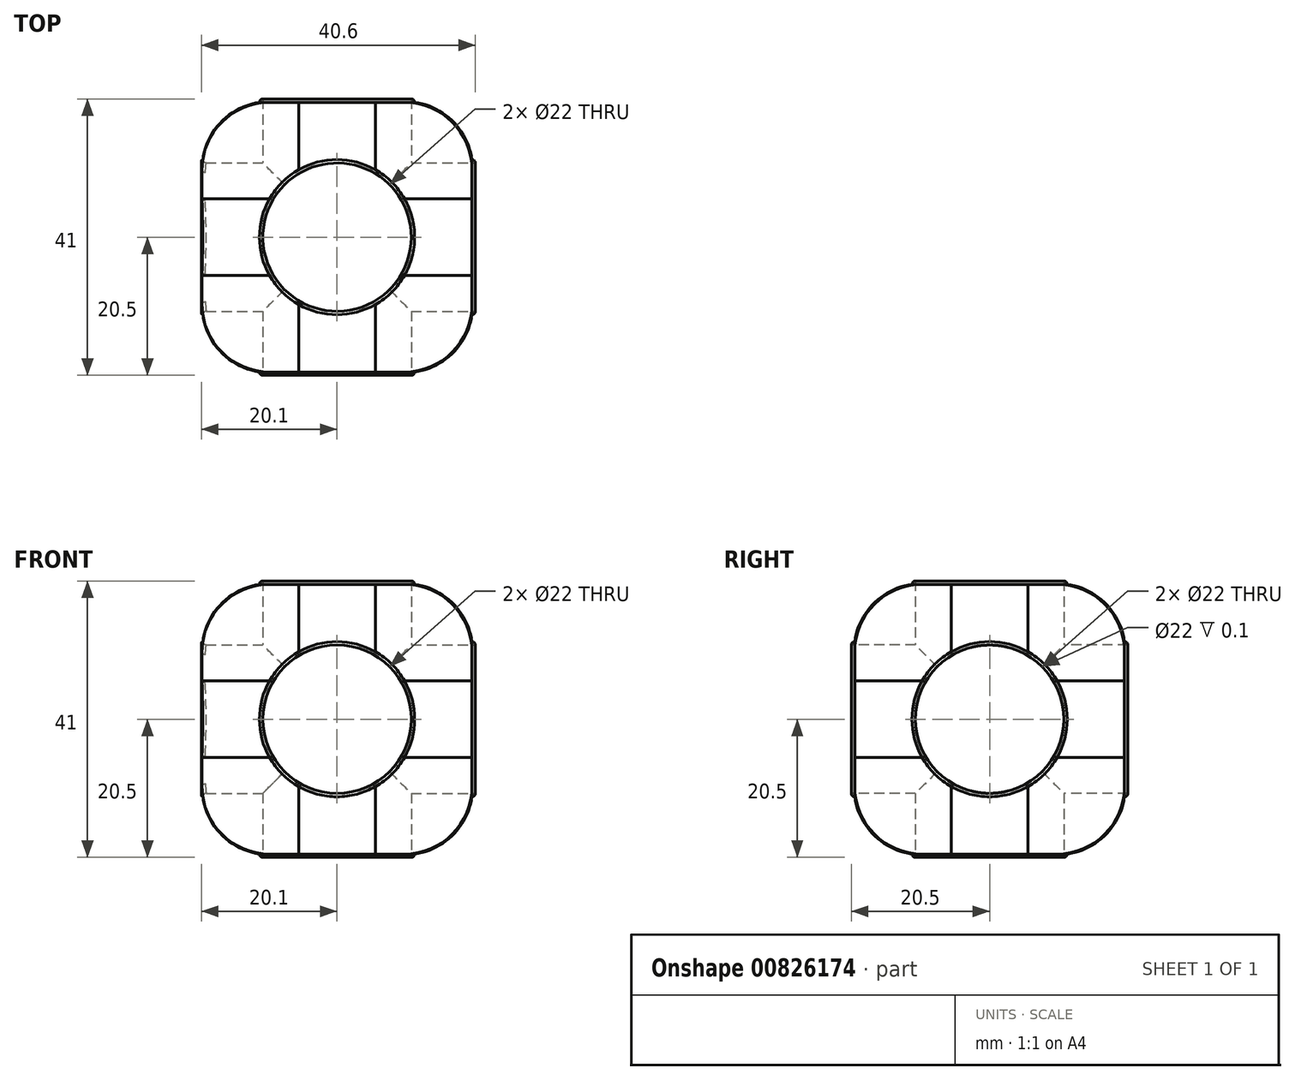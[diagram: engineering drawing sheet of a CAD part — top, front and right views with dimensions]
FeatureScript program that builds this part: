
annotation { "Feature Type Name" : "Feature", "Feature Type Description" : "" }
export const myFeature = defineFeature(function(context is Context, id is Id, definition is map)
    precondition{}
    {
        {
            var Q0;
            Q0=qCreatedBy(makeId("Top.planeOp"),FACE);
            var sketch = newSketch(context, id + "F0", { "sketchPlane" : qUnion([Q0])});
            skCircle(sketch, "E0", {"center": v(0, 0) * mm, "radius": 11 * mm});
            skLineSegment(sketch, "E1", {"start": v(0, 20) * mm, "end": v(20, 20) * mm});
            skLineSegment(sketch, "E2.MirrorCS", {"start": v(0, -20) * mm, "end": v(20, -20) * mm});
            skLineSegment(sketch, "E3", {"start": v(20, 20) * mm, "end": v(20, -20) * mm});
            skLineSegment(sketch, "E4.MirrorCS", {"start": v(-20, 20) * mm, "end": v(-20, -20) * mm});
            skLineSegment(sketch, "E5.MirrorCS", {"start": v(0, 20) * mm, "end": v(-20, 20) * mm});
            skLineSegment(sketch, "E6.MirrorCS", {"start": v(0, -20) * mm, "end": v(-20, -20) * mm});
            skPoint(sketch, "E7.orphan", {"position": v(0, 20) * mm});
            skPoint(sketch, "E8.MirrorCS.end.orphan", {"position": v(0, -20) * mm});
            skSolve(sketch);
        }
        {
            var Q0;
            Q0 = qSketchRegion(id + "F0", true);
            extrude(context, id + "F1", {"entities" : qUnion([Q0]), "depth" : 40 * mm, "offsetDistance" : 25 * mm});
        }
        {
            var Q0;
            Q0=makeQuery(id+"F1.opExtrude","SWEPT_FACE",FACE,{"disambiguationData":[OSD([sQuery(id+"F0.wireOp",EDGE,"E3")])]});
            var sketch = newSketch(context, id + "F2", { "sketchPlane" : qUnion([Q0])});
            skCircle(sketch, "E9", {"center": v(0, 20) * mm, "radius": 11 * mm});
            skPoint(sketch, "E10.orphan", {"position": v(20, 20) * mm});
            skPoint(sketch, "E11.end.orphan", {"position": v(-20, 20) * mm});
            skPoint(sketch, "E12.trimOffspring.end.orphan", {"position": v(0, 0) * mm});
            skPoint(sketch, "E13.start.orphan", {"position": v(0, 40) * mm});
            skSolve(sketch);
        }
        {
            var Q0;
            Q0 = qSketchRegion(id + "F2", true);
            var Q1;
            Q1=sQuery(id+"F2.wireOp",EDGE,"E9");
            extrude(context, id + "F3", {"entities" : qUnion([Q0]), "operationType" : NewBodyOperationType.REMOVE, "surfaceEntities" : qUnion([Q1]), "oppositeDirection" : true, "depth" : 40 * mm, "offsetDistance" : 25 * mm});
        }
        {
            var Q0;
            Q0=makeQuery(id+"F1.opExtrude","SWEPT_FACE",FACE,{"disambiguationData":[OSD([sQuery(id+"F0.wireOp",EDGE,"E2.MirrorCS"),sQuery(id+"F0.wireOp",EDGE,"E6.MirrorCS")])]});
            var sketch = newSketch(context, id + "F4", { "sketchPlane" : qUnion([Q0])});
            skCircle(sketch, "E14", {"center": v(0, 20) * mm, "radius": 11 * mm});
            skPoint(sketch, "E15.orphan", {"position": v(-20, 20) * mm});
            skPoint(sketch, "E16.end.orphan", {"position": v(20, 20) * mm});
            skPoint(sketch, "E17.start.orphan", {"position": v(0, 0) * mm});
            skPoint(sketch, "E18.trimOffspring.end.orphan", {"position": v(0, 40) * mm});
            skSolve(sketch);
        }
        {
            var Q0;
            Q0=makeQuery(id+"F4.imprint","IMPRINT",FACE,{"disambiguationData":[TD([[makeQuery(id+"F4.imprint","IMPRINT",EDGE,{"derivedFrom":sQuery(id+"F4.wireOp",EDGE,"E14")}),1.0]])]});
            var Q1;
            Q1=sQuery(id+"F4.wireOp",EDGE,"E14");
            extrude(context, id + "F5", {"entities" : qUnion([Q0]), "operationType" : NewBodyOperationType.REMOVE, "surfaceEntities" : qUnion([Q1]), "oppositeDirection" : true, "depth" : 40 * mm, "offsetDistance" : 25 * mm});
        }
        {
            var Q0;
            Q0=makeQuery(id+"F1.opExtrude","SWEPT_FACE",FACE,{"disambiguationData":[OSD([sQuery(id+"F0.wireOp",EDGE,"E4.MirrorCS")])]});
            var sketch = newSketch(context, id + "F6", { "sketchPlane" : qUnion([Q0])});
            skCircle(sketch, "E19", {"center": v(0, 20) * mm, "radius": 11 * mm});
            skCircle(sketch, "E20", {"center": v(0, 20) * mm, "radius": 11.5 * mm});
            skSolve(sketch);
        }
        {
            var Q0;
            Q0 = qSketchRegion(id + "F6", true);
            extrude(context, id + "F7", {"entities" : qUnion([Q0]), "depth" : 0.1 * mm, "offsetDistance" : 25 * mm});
        }
        {
            var Q0;
            Q0=makeQuery(id+"F1.opExtrude","SWEPT_FACE",FACE,{"disambiguationData":[OSD([sQuery(id+"F0.wireOp",EDGE,"E2.MirrorCS"),sQuery(id+"F0.wireOp",EDGE,"E6.MirrorCS")])]});
            var sketch = newSketch(context, id + "F8", { "sketchPlane" : qUnion([Q0])});
            skCircle(sketch, "E21", {"center": v(0, 20) * mm, "radius": 11 * mm});
            skCircle(sketch, "E22", {"center": v(0, 20) * mm, "radius": 11.5 * mm});
            skSolve(sketch);
        }
        {
            var Q0;
            Q0 = qSketchRegion(id + "F8", true);
            extrude(context, id + "F9", {"entities" : qUnion([Q0]), "operationType" : NewBodyOperationType.ADD, "depth" : 0.5 * mm, "offsetDistance" : 25 * mm});
        }
        {
            var Q0;
            Q0=makeQuery(id+"F1.opExtrude","SWEPT_FACE",FACE,{"disambiguationData":[OSD([sQuery(id+"F0.wireOp",EDGE,"E3")])]});
            var sketch = newSketch(context, id + "F10", { "sketchPlane" : qUnion([Q0])});
            skCircle(sketch, "E23", {"center": v(0, 20) * mm, "radius": 11 * mm});
            skCircle(sketch, "E24", {"center": v(0, 20) * mm, "radius": 11.5 * mm});
            skSolve(sketch);
        }
        {
            var Q0;
            Q0=makeQuery(id+"F10.imprint","IMPRINT",FACE,{"disambiguationData":[TD([[makeQuery(id+"F10.imprint","IMPRINT",EDGE,{"derivedFrom":sQuery(id+"F10.wireOp",EDGE,"E23")}),-1.0]])]});
            extrude(context, id + "F11", {"entities" : qUnion([Q0]), "operationType" : NewBodyOperationType.ADD, "depth" : 0.5 * mm, "offsetDistance" : 25 * mm});
        }
        {
            var Q0;
            Q0=makeQuery(id+"F1.opExtrude","SWEPT_FACE",FACE,{"disambiguationData":[OSD([sQuery(id+"F0.wireOp",EDGE,"E1"),sQuery(id+"F0.wireOp",EDGE,"E5.MirrorCS")])]});
            var sketch = newSketch(context, id + "F12", { "sketchPlane" : qUnion([Q0])});
            skCircle(sketch, "E25", {"center": v(0, 20) * mm, "radius": 11 * mm});
            skCircle(sketch, "E26", {"center": v(0, 20) * mm, "radius": 11.5 * mm});
            skSolve(sketch);
        }
        {
            var Q0;
            Q0 = qSketchRegion(id + "F12", true);
            extrude(context, id + "F13", {"entities" : qUnion([Q0]), "operationType" : NewBodyOperationType.ADD, "depth" : 0.5 * mm, "offsetDistance" : 25 * mm});
        }
        {
            var Q0;
            Q0=makeQuery(id+"F1.opExtrude","CAP_FACE",FACE,{"disambiguationData":[OSD([sQuery(id+"F0.wireOp",EDGE,"E0"),sQuery(id+"F0.wireOp",EDGE,"E1"),sQuery(id+"F0.wireOp",EDGE,"E2.MirrorCS"),sQuery(id+"F0.wireOp",EDGE,"E3"),sQuery(id+"F0.wireOp",EDGE,"E4.MirrorCS"),sQuery(id+"F0.wireOp",EDGE,"E5.MirrorCS"),sQuery(id+"F0.wireOp",EDGE,"E6.MirrorCS")])],"isStart":true});
            var sketch = newSketch(context, id + "F14", { "sketchPlane" : qUnion([Q0])});
            skCircle(sketch, "E27", {"center": v(0, 0) * mm, "radius": 11 * mm});
            skCircle(sketch, "E28", {"center": v(0, 0) * mm, "radius": 11.5 * mm});
            skSolve(sketch);
        }
        {
            var Q0;
            Q0 = qSketchRegion(id + "F14", true);
            extrude(context, id + "F15", {"entities" : qUnion([Q0]), "operationType" : NewBodyOperationType.ADD, "depth" : 0.5 * mm, "offsetDistance" : 25 * mm});
        }
        {
            var Q0;
            Q0=makeQuery(id+"F1.opExtrude","CAP_FACE",FACE,{"disambiguationData":[OSD([sQuery(id+"F0.wireOp",EDGE,"E0"),sQuery(id+"F0.wireOp",EDGE,"E1"),sQuery(id+"F0.wireOp",EDGE,"E2.MirrorCS"),sQuery(id+"F0.wireOp",EDGE,"E3"),sQuery(id+"F0.wireOp",EDGE,"E4.MirrorCS"),sQuery(id+"F0.wireOp",EDGE,"E5.MirrorCS"),sQuery(id+"F0.wireOp",EDGE,"E6.MirrorCS")])],"isStart":false});
            var sketch = newSketch(context, id + "F16", { "sketchPlane" : qUnion([Q0])});
            skCircle(sketch, "E29", {"center": v(0, 0) * mm, "radius": 11 * mm});
            skCircle(sketch, "E30", {"center": v(0, 0) * mm, "radius": 11.5 * mm});
            skSolve(sketch);
        }
        {
            var Q0;
            Q0 = qSketchRegion(id + "F16", true);
            extrude(context, id + "F17", {"entities" : qUnion([Q0]), "operationType" : NewBodyOperationType.ADD, "depth" : 0.5 * mm, "offsetDistance" : 25 * mm});
        }
        {
            var Q0;
            Q0=makeQuery(id+"F1.opExtrude","SWEPT_EDGE",EDGE,{"disambiguationData":[OSD([sQuery(id+"F0.wireOp",EDGE,"E2.MirrorCS"),sQuery(id+"F0.wireOp",EDGE,"E3")])]});
            var Q1;
            Q1=makeQuery(id+"F1.opExtrude","CAP_EDGE",EDGE,{"disambiguationData":[OSD([sQuery(id+"F0.wireOp",EDGE,"E3")])],"isStart":true});
            var Q2;
            Q2=makeQuery(id+"F1.opExtrude","SWEPT_EDGE",EDGE,{"disambiguationData":[OSD([sQuery(id+"F0.wireOp",EDGE,"E1"),sQuery(id+"F0.wireOp",EDGE,"E3")])]});
            var Q3;
            Q3=makeQuery(id+"F1.opExtrude","CAP_EDGE",EDGE,{"disambiguationData":[OSD([sQuery(id+"F0.wireOp",EDGE,"E3")])],"isStart":false});
            var Q4;
            Q4=makeQuery(id+"F1.opExtrude","CAP_EDGE",EDGE,{"disambiguationData":[OSD([sQuery(id+"F0.wireOp",EDGE,"E2.MirrorCS"),sQuery(id+"F0.wireOp",EDGE,"E6.MirrorCS")])],"isStart":false});
            var Q5;
            Q5=makeQuery(id+"F1.opExtrude","CAP_EDGE",EDGE,{"disambiguationData":[OSD([sQuery(id+"F0.wireOp",EDGE,"E1"),sQuery(id+"F0.wireOp",EDGE,"E5.MirrorCS")])],"isStart":false});
            var Q6;
            Q6=makeQuery(id+"F1.opExtrude","CAP_EDGE",EDGE,{"disambiguationData":[OSD([sQuery(id+"F0.wireOp",EDGE,"E2.MirrorCS"),sQuery(id+"F0.wireOp",EDGE,"E6.MirrorCS")])],"isStart":true});
            var Q7;
            Q7=makeQuery(id+"F1.opExtrude","CAP_EDGE",EDGE,{"disambiguationData":[OSD([sQuery(id+"F0.wireOp",EDGE,"E1"),sQuery(id+"F0.wireOp",EDGE,"E5.MirrorCS")])],"isStart":true});
            var Q8;
            Q8=makeQuery(id+"F1.opExtrude","CAP_EDGE",EDGE,{"disambiguationData":[OSD([sQuery(id+"F0.wireOp",EDGE,"E4.MirrorCS")])],"isStart":true});
            var Q9;
            Q9=makeQuery(id+"F1.opExtrude","SWEPT_EDGE",EDGE,{"disambiguationData":[OSD([sQuery(id+"F0.wireOp",EDGE,"E4.MirrorCS"),sQuery(id+"F0.wireOp",EDGE,"E5.MirrorCS")])]});
            var Q10;
            Q10=makeQuery(id+"F1.opExtrude","SWEPT_EDGE",EDGE,{"disambiguationData":[OSD([sQuery(id+"F0.wireOp",EDGE,"E4.MirrorCS"),sQuery(id+"F0.wireOp",EDGE,"E6.MirrorCS")])]});
            var Q11;
            Q11=makeQuery(id+"F1.opExtrude","CAP_EDGE",EDGE,{"disambiguationData":[OSD([sQuery(id+"F0.wireOp",EDGE,"E4.MirrorCS")])],"isStart":false});
            fillet(context, id + "F18", {"entities" : qUnion([Q0, Q1, Q2, Q3, Q4, Q5, Q6, Q7, Q8, Q9, Q10, Q11]), "radius" : 10 * mm, "tangentPropagation" : true, "allowEdgeOverflow" : false});
        }
        {
            var Q0;
            {var subQ0=sQuery(id+"F0.wireOp",EDGE,"E3");var subQ1=makeQuery(id+"F3.opExtrude","SWEPT_FACE",FACE,{"disambiguationData":[OSD([sQuery(id+"F2.wireOp",EDGE,"E9")])]});Q0=makeQuery(id+"F18.opFillet","BLEND_EDGE",EDGE,{"blendedFrom":[makeQuery(id+"F1.opExtrude","CAP_EDGE",EDGE,{"disambiguationData":[OSD([subQ0])],"isStart":false}),makeQuery(id+"F3.boolean.opBoolean","COPY",FACE,{"disambiguationData":[TD([makeQuery(id+"F1.opExtrude","SWEPT_FACE",FACE,{"disambiguationData":[OSD([subQ0])]})])],"derivedFrom":subQ1})],"blendedInto":[makeQuery(id+"F3.boolean.opBoolean","COPY",FACE,{"disambiguationData":[TD([makeQuery(id+"F1.opExtrude","SWEPT_FACE",FACE,{"disambiguationData":[OSD([subQ0])]})])],"derivedFrom":subQ1})]});}
            var Q1;
            {var subQ0=sQuery(id+"F0.wireOp",EDGE,"E3");var subQ1=makeQuery(id+"F3.opExtrude","SWEPT_FACE",FACE,{"disambiguationData":[OSD([sQuery(id+"F2.wireOp",EDGE,"E9")])]});Q1=makeQuery(id+"F18.opFillet","BLEND_EDGE",EDGE,{"blendedFrom":[makeQuery(id+"F1.opExtrude","SWEPT_EDGE",EDGE,{"disambiguationData":[OSD([sQuery(id+"F0.wireOp",EDGE,"E2.MirrorCS"),subQ0])]}),makeQuery(id+"F3.boolean.opBoolean","COPY",FACE,{"disambiguationData":[TD([makeQuery(id+"F1.opExtrude","SWEPT_FACE",FACE,{"disambiguationData":[OSD([subQ0])]})])],"derivedFrom":subQ1})],"blendedInto":[makeQuery(id+"F3.boolean.opBoolean","COPY",FACE,{"disambiguationData":[TD([makeQuery(id+"F1.opExtrude","SWEPT_FACE",FACE,{"disambiguationData":[OSD([subQ0])]})])],"derivedFrom":subQ1})]});}
            var Q2;
            {var subQ0=sQuery(id+"F0.wireOp",EDGE,"E3");var subQ1=makeQuery(id+"F3.opExtrude","SWEPT_FACE",FACE,{"disambiguationData":[OSD([sQuery(id+"F2.wireOp",EDGE,"E9")])]});Q2=makeQuery(id+"F18.opFillet","BLEND_EDGE",EDGE,{"blendedFrom":[makeQuery(id+"F1.opExtrude","CAP_EDGE",EDGE,{"disambiguationData":[OSD([subQ0])],"isStart":true}),makeQuery(id+"F3.boolean.opBoolean","COPY",FACE,{"disambiguationData":[TD([makeQuery(id+"F1.opExtrude","SWEPT_FACE",FACE,{"disambiguationData":[OSD([subQ0])]})])],"derivedFrom":subQ1})],"blendedInto":[makeQuery(id+"F3.boolean.opBoolean","COPY",FACE,{"disambiguationData":[TD([makeQuery(id+"F1.opExtrude","SWEPT_FACE",FACE,{"disambiguationData":[OSD([subQ0])]})])],"derivedFrom":subQ1})]});}
            var Q3;
            {var subQ0=sQuery(id+"F0.wireOp",EDGE,"E3");var subQ1=makeQuery(id+"F3.opExtrude","SWEPT_FACE",FACE,{"disambiguationData":[OSD([sQuery(id+"F2.wireOp",EDGE,"E9")])]});Q3=makeQuery(id+"F18.opFillet","BLEND_EDGE",EDGE,{"blendedFrom":[makeQuery(id+"F1.opExtrude","SWEPT_EDGE",EDGE,{"disambiguationData":[OSD([sQuery(id+"F0.wireOp",EDGE,"E1"),subQ0])]}),makeQuery(id+"F3.boolean.opBoolean","COPY",FACE,{"disambiguationData":[TD([makeQuery(id+"F1.opExtrude","SWEPT_FACE",FACE,{"disambiguationData":[OSD([subQ0])]})])],"derivedFrom":subQ1})],"blendedInto":[makeQuery(id+"F3.boolean.opBoolean","COPY",FACE,{"disambiguationData":[TD([makeQuery(id+"F1.opExtrude","SWEPT_FACE",FACE,{"disambiguationData":[OSD([subQ0])]})])],"derivedFrom":subQ1})]});}
            var Q4;
            {var subQ1=sQuery(id+"F0.wireOp",EDGE,"E6.MirrorCS");var subQ2=sQuery(id+"F0.wireOp",EDGE,"E2.MirrorCS");Q4=makeQuery(id+"F18.opFillet","BLEND_EDGE",EDGE,{"blendedFrom":[makeQuery(id+"F1.opExtrude","CAP_EDGE",EDGE,{"disambiguationData":[OSD([subQ2,subQ1])],"isStart":true}),makeQuery(id+"F5.boolean.opBoolean","COPY",FACE,{"disambiguationData":[TD([makeQuery(id+"F1.opExtrude","SWEPT_FACE",FACE,{"disambiguationData":[OSD([subQ2,subQ1])]})])],"derivedFrom":makeQuery(id+"F5.opExtrude","SWEPT_FACE",FACE,{"disambiguationData":[OSD([sQuery(id+"F4.wireOp",EDGE,"E14")])]})})],"blendedInto":[makeQuery(id+"F5.boolean.opBoolean","COPY",FACE,{"disambiguationData":[TD([makeQuery(id+"F1.opExtrude","SWEPT_FACE",FACE,{"disambiguationData":[OSD([subQ2,subQ1])]})])],"derivedFrom":makeQuery(id+"F5.opExtrude","SWEPT_FACE",FACE,{"disambiguationData":[OSD([sQuery(id+"F4.wireOp",EDGE,"E14")])]})})]});}
            var Q5;
            {var subQ1=sQuery(id+"F0.wireOp",EDGE,"E2.MirrorCS");var subQ3=sQuery(id+"F0.wireOp",EDGE,"E3");Q5=makeQuery(id+"F18.opFillet","BLEND_EDGE",EDGE,{"blendedFrom":[makeQuery(id+"F1.opExtrude","SWEPT_EDGE",EDGE,{"disambiguationData":[OSD([subQ1,subQ3])]}),makeQuery(id+"F5.boolean.opBoolean","COPY",FACE,{"disambiguationData":[TD([makeQuery(id+"F1.opExtrude","SWEPT_FACE",FACE,{"disambiguationData":[OSD([subQ1,sQuery(id+"F0.wireOp",EDGE,"E6.MirrorCS")])]})])],"derivedFrom":makeQuery(id+"F5.opExtrude","SWEPT_FACE",FACE,{"disambiguationData":[OSD([sQuery(id+"F4.wireOp",EDGE,"E14")])]})})],"blendedInto":[makeQuery(id+"F5.boolean.opBoolean","COPY",FACE,{"disambiguationData":[TD([makeQuery(id+"F1.opExtrude","SWEPT_FACE",FACE,{"disambiguationData":[OSD([subQ1,sQuery(id+"F0.wireOp",EDGE,"E6.MirrorCS")])]})])],"derivedFrom":makeQuery(id+"F5.opExtrude","SWEPT_FACE",FACE,{"disambiguationData":[OSD([sQuery(id+"F4.wireOp",EDGE,"E14")])]})})]});}
            var Q6;
            {var subQ1=sQuery(id+"F0.wireOp",EDGE,"E6.MirrorCS");var subQ2=sQuery(id+"F0.wireOp",EDGE,"E2.MirrorCS");Q6=makeQuery(id+"F18.opFillet","BLEND_EDGE",EDGE,{"blendedFrom":[makeQuery(id+"F1.opExtrude","CAP_EDGE",EDGE,{"disambiguationData":[OSD([subQ2,subQ1])],"isStart":false}),makeQuery(id+"F5.boolean.opBoolean","COPY",FACE,{"disambiguationData":[TD([makeQuery(id+"F1.opExtrude","SWEPT_FACE",FACE,{"disambiguationData":[OSD([subQ2,subQ1])]})])],"derivedFrom":makeQuery(id+"F5.opExtrude","SWEPT_FACE",FACE,{"disambiguationData":[OSD([sQuery(id+"F4.wireOp",EDGE,"E14")])]})})],"blendedInto":[makeQuery(id+"F5.boolean.opBoolean","COPY",FACE,{"disambiguationData":[TD([makeQuery(id+"F1.opExtrude","SWEPT_FACE",FACE,{"disambiguationData":[OSD([subQ2,subQ1])]})])],"derivedFrom":makeQuery(id+"F5.opExtrude","SWEPT_FACE",FACE,{"disambiguationData":[OSD([sQuery(id+"F4.wireOp",EDGE,"E14")])]})})]});}
            var Q7;
            {var subQ1=sQuery(id+"F0.wireOp",EDGE,"E6.MirrorCS");var subQ2=sQuery(id+"F0.wireOp",EDGE,"E4.MirrorCS");Q7=makeQuery(id+"F18.opFillet","BLEND_EDGE",EDGE,{"blendedFrom":[makeQuery(id+"F1.opExtrude","SWEPT_EDGE",EDGE,{"disambiguationData":[OSD([subQ2,subQ1])]}),makeQuery(id+"F5.boolean.opBoolean","COPY",FACE,{"disambiguationData":[TD([makeQuery(id+"F1.opExtrude","SWEPT_FACE",FACE,{"disambiguationData":[OSD([sQuery(id+"F0.wireOp",EDGE,"E2.MirrorCS"),subQ1])]})])],"derivedFrom":makeQuery(id+"F5.opExtrude","SWEPT_FACE",FACE,{"disambiguationData":[OSD([sQuery(id+"F4.wireOp",EDGE,"E14")])]})})],"blendedInto":[makeQuery(id+"F5.boolean.opBoolean","COPY",FACE,{"disambiguationData":[TD([makeQuery(id+"F1.opExtrude","SWEPT_FACE",FACE,{"disambiguationData":[OSD([sQuery(id+"F0.wireOp",EDGE,"E2.MirrorCS"),subQ1])]})])],"derivedFrom":makeQuery(id+"F5.opExtrude","SWEPT_FACE",FACE,{"disambiguationData":[OSD([sQuery(id+"F4.wireOp",EDGE,"E14")])]})})]});}
            var Q8;
            {var subQ0=sQuery(id+"F0.wireOp",EDGE,"E4.MirrorCS");var subQ1=makeQuery(id+"F3.opExtrude","SWEPT_FACE",FACE,{"disambiguationData":[OSD([sQuery(id+"F2.wireOp",EDGE,"E9")])]});Q8=makeQuery(id+"F18.opFillet","BLEND_EDGE",EDGE,{"blendedFrom":[makeQuery(id+"F1.opExtrude","CAP_EDGE",EDGE,{"disambiguationData":[OSD([subQ0])],"isStart":true}),makeQuery(id+"F3.boolean.opBoolean","COPY",FACE,{"disambiguationData":[TD([makeQuery(id+"F1.opExtrude","SWEPT_FACE",FACE,{"disambiguationData":[OSD([subQ0])]})])],"derivedFrom":subQ1})],"blendedInto":[makeQuery(id+"F3.boolean.opBoolean","COPY",FACE,{"disambiguationData":[TD([makeQuery(id+"F1.opExtrude","SWEPT_FACE",FACE,{"disambiguationData":[OSD([subQ0])]})])],"derivedFrom":subQ1})]});}
            var Q9;
            {var subQ0=sQuery(id+"F0.wireOp",EDGE,"E4.MirrorCS");var subQ1=makeQuery(id+"F3.opExtrude","SWEPT_FACE",FACE,{"disambiguationData":[OSD([sQuery(id+"F2.wireOp",EDGE,"E9")])]});Q9=makeQuery(id+"F18.opFillet","BLEND_EDGE",EDGE,{"blendedFrom":[makeQuery(id+"F1.opExtrude","SWEPT_EDGE",EDGE,{"disambiguationData":[OSD([subQ0,sQuery(id+"F0.wireOp",EDGE,"E5.MirrorCS")])]}),makeQuery(id+"F3.boolean.opBoolean","COPY",FACE,{"disambiguationData":[TD([makeQuery(id+"F1.opExtrude","SWEPT_FACE",FACE,{"disambiguationData":[OSD([subQ0])]})])],"derivedFrom":subQ1})],"blendedInto":[makeQuery(id+"F3.boolean.opBoolean","COPY",FACE,{"disambiguationData":[TD([makeQuery(id+"F1.opExtrude","SWEPT_FACE",FACE,{"disambiguationData":[OSD([subQ0])]})])],"derivedFrom":subQ1})]});}
            var Q10;
            {var subQ0=sQuery(id+"F0.wireOp",EDGE,"E4.MirrorCS");var subQ1=makeQuery(id+"F3.opExtrude","SWEPT_FACE",FACE,{"disambiguationData":[OSD([sQuery(id+"F2.wireOp",EDGE,"E9")])]});Q10=makeQuery(id+"F18.opFillet","BLEND_EDGE",EDGE,{"blendedFrom":[makeQuery(id+"F1.opExtrude","CAP_EDGE",EDGE,{"disambiguationData":[OSD([subQ0])],"isStart":false}),makeQuery(id+"F3.boolean.opBoolean","COPY",FACE,{"disambiguationData":[TD([makeQuery(id+"F1.opExtrude","SWEPT_FACE",FACE,{"disambiguationData":[OSD([subQ0])]})])],"derivedFrom":subQ1})],"blendedInto":[makeQuery(id+"F3.boolean.opBoolean","COPY",FACE,{"disambiguationData":[TD([makeQuery(id+"F1.opExtrude","SWEPT_FACE",FACE,{"disambiguationData":[OSD([subQ0])]})])],"derivedFrom":subQ1})]});}
            var Q11;
            {var subQ0=sQuery(id+"F0.wireOp",EDGE,"E4.MirrorCS");var subQ1=makeQuery(id+"F3.opExtrude","SWEPT_FACE",FACE,{"disambiguationData":[OSD([sQuery(id+"F2.wireOp",EDGE,"E9")])]});Q11=makeQuery(id+"F18.opFillet","BLEND_EDGE",EDGE,{"blendedFrom":[makeQuery(id+"F1.opExtrude","SWEPT_EDGE",EDGE,{"disambiguationData":[OSD([subQ0,sQuery(id+"F0.wireOp",EDGE,"E6.MirrorCS")])]}),makeQuery(id+"F3.boolean.opBoolean","COPY",FACE,{"disambiguationData":[TD([makeQuery(id+"F1.opExtrude","SWEPT_FACE",FACE,{"disambiguationData":[OSD([subQ0])]})])],"derivedFrom":subQ1})],"blendedInto":[makeQuery(id+"F3.boolean.opBoolean","COPY",FACE,{"disambiguationData":[TD([makeQuery(id+"F1.opExtrude","SWEPT_FACE",FACE,{"disambiguationData":[OSD([subQ0])]})])],"derivedFrom":subQ1})]});}
            var Q12;
            {var subQ0=sQuery(id+"F0.wireOp",EDGE,"E0");var subQ1=makeQuery(id+"F1.opExtrude","SWEPT_FACE",FACE,{"disambiguationData":[OSD([subQ0])]});var subQ2=sQuery(id+"F0.wireOp",EDGE,"E4.MirrorCS");Q12=makeQuery(id+"F18.opFillet","BLEND_EDGE",EDGE,{"blendedFrom":[makeQuery(id+"F1.opExtrude","CAP_EDGE",EDGE,{"disambiguationData":[OSD([subQ2])],"isStart":false}),makeQuery(id+"F3.boolean.opBoolean","SPLIT",FACE,{"disambiguationData":[TD([makeQuery(id+"F1.opExtrude","CAP_FACE",FACE,{"disambiguationData":[OSD([subQ0,sQuery(id+"F0.wireOp",EDGE,"E1"),sQuery(id+"F0.wireOp",EDGE,"E2.MirrorCS"),sQuery(id+"F0.wireOp",EDGE,"E3"),subQ2,sQuery(id+"F0.wireOp",EDGE,"E5.MirrorCS"),sQuery(id+"F0.wireOp",EDGE,"E6.MirrorCS")])],"isStart":false})])],"derivedFrom":subQ1})],"blendedInto":[makeQuery(id+"F3.boolean.opBoolean","SPLIT",FACE,{"disambiguationData":[TD([makeQuery(id+"F1.opExtrude","CAP_FACE",FACE,{"disambiguationData":[OSD([subQ0,sQuery(id+"F0.wireOp",EDGE,"E1"),sQuery(id+"F0.wireOp",EDGE,"E2.MirrorCS"),sQuery(id+"F0.wireOp",EDGE,"E3"),subQ2,sQuery(id+"F0.wireOp",EDGE,"E5.MirrorCS"),sQuery(id+"F0.wireOp",EDGE,"E6.MirrorCS")])],"isStart":false})])],"derivedFrom":subQ1})]});}
            var Q13;
            {var subQ0=sQuery(id+"F0.wireOp",EDGE,"E0");var subQ1=makeQuery(id+"F1.opExtrude","SWEPT_FACE",FACE,{"disambiguationData":[OSD([subQ0])]});var subQ2=sQuery(id+"F0.wireOp",EDGE,"E5.MirrorCS");var subQ3=sQuery(id+"F0.wireOp",EDGE,"E1");Q13=makeQuery(id+"F18.opFillet","BLEND_EDGE",EDGE,{"blendedFrom":[makeQuery(id+"F1.opExtrude","CAP_EDGE",EDGE,{"disambiguationData":[OSD([subQ3,subQ2])],"isStart":false}),makeQuery(id+"F3.boolean.opBoolean","SPLIT",FACE,{"disambiguationData":[TD([makeQuery(id+"F1.opExtrude","CAP_FACE",FACE,{"disambiguationData":[OSD([subQ0,subQ3,sQuery(id+"F0.wireOp",EDGE,"E2.MirrorCS"),sQuery(id+"F0.wireOp",EDGE,"E3"),sQuery(id+"F0.wireOp",EDGE,"E4.MirrorCS"),subQ2,sQuery(id+"F0.wireOp",EDGE,"E6.MirrorCS")])],"isStart":false})])],"derivedFrom":subQ1})],"blendedInto":[makeQuery(id+"F3.boolean.opBoolean","SPLIT",FACE,{"disambiguationData":[TD([makeQuery(id+"F1.opExtrude","CAP_FACE",FACE,{"disambiguationData":[OSD([subQ0,subQ3,sQuery(id+"F0.wireOp",EDGE,"E2.MirrorCS"),sQuery(id+"F0.wireOp",EDGE,"E3"),sQuery(id+"F0.wireOp",EDGE,"E4.MirrorCS"),subQ2,sQuery(id+"F0.wireOp",EDGE,"E6.MirrorCS")])],"isStart":false})])],"derivedFrom":subQ1})]});}
            var Q14;
            {var subQ0=sQuery(id+"F0.wireOp",EDGE,"E0");var subQ1=makeQuery(id+"F1.opExtrude","SWEPT_FACE",FACE,{"disambiguationData":[OSD([subQ0])]});var subQ2=sQuery(id+"F0.wireOp",EDGE,"E3");Q14=makeQuery(id+"F18.opFillet","BLEND_EDGE",EDGE,{"blendedFrom":[makeQuery(id+"F1.opExtrude","CAP_EDGE",EDGE,{"disambiguationData":[OSD([subQ2])],"isStart":false}),makeQuery(id+"F3.boolean.opBoolean","SPLIT",FACE,{"disambiguationData":[TD([makeQuery(id+"F1.opExtrude","CAP_FACE",FACE,{"disambiguationData":[OSD([subQ0,sQuery(id+"F0.wireOp",EDGE,"E1"),sQuery(id+"F0.wireOp",EDGE,"E2.MirrorCS"),subQ2,sQuery(id+"F0.wireOp",EDGE,"E4.MirrorCS"),sQuery(id+"F0.wireOp",EDGE,"E5.MirrorCS"),sQuery(id+"F0.wireOp",EDGE,"E6.MirrorCS")])],"isStart":false})])],"derivedFrom":subQ1})],"blendedInto":[makeQuery(id+"F3.boolean.opBoolean","SPLIT",FACE,{"disambiguationData":[TD([makeQuery(id+"F1.opExtrude","CAP_FACE",FACE,{"disambiguationData":[OSD([subQ0,sQuery(id+"F0.wireOp",EDGE,"E1"),sQuery(id+"F0.wireOp",EDGE,"E2.MirrorCS"),subQ2,sQuery(id+"F0.wireOp",EDGE,"E4.MirrorCS"),sQuery(id+"F0.wireOp",EDGE,"E5.MirrorCS"),sQuery(id+"F0.wireOp",EDGE,"E6.MirrorCS")])],"isStart":false})])],"derivedFrom":subQ1})]});}
            var Q15;
            {var subQ0=sQuery(id+"F0.wireOp",EDGE,"E0");var subQ1=makeQuery(id+"F1.opExtrude","SWEPT_FACE",FACE,{"disambiguationData":[OSD([subQ0])]});var subQ2=sQuery(id+"F0.wireOp",EDGE,"E6.MirrorCS");var subQ3=sQuery(id+"F0.wireOp",EDGE,"E2.MirrorCS");Q15=makeQuery(id+"F18.opFillet","BLEND_EDGE",EDGE,{"blendedFrom":[makeQuery(id+"F1.opExtrude","CAP_EDGE",EDGE,{"disambiguationData":[OSD([subQ3,subQ2])],"isStart":false}),makeQuery(id+"F3.boolean.opBoolean","SPLIT",FACE,{"disambiguationData":[TD([makeQuery(id+"F1.opExtrude","CAP_FACE",FACE,{"disambiguationData":[OSD([subQ0,sQuery(id+"F0.wireOp",EDGE,"E1"),subQ3,sQuery(id+"F0.wireOp",EDGE,"E3"),sQuery(id+"F0.wireOp",EDGE,"E4.MirrorCS"),sQuery(id+"F0.wireOp",EDGE,"E5.MirrorCS"),subQ2])],"isStart":false})])],"derivedFrom":subQ1})],"blendedInto":[makeQuery(id+"F3.boolean.opBoolean","SPLIT",FACE,{"disambiguationData":[TD([makeQuery(id+"F1.opExtrude","CAP_FACE",FACE,{"disambiguationData":[OSD([subQ0,sQuery(id+"F0.wireOp",EDGE,"E1"),subQ3,sQuery(id+"F0.wireOp",EDGE,"E3"),sQuery(id+"F0.wireOp",EDGE,"E4.MirrorCS"),sQuery(id+"F0.wireOp",EDGE,"E5.MirrorCS"),subQ2])],"isStart":false})])],"derivedFrom":subQ1})]});}
            var Q16;
            {var subQ1=sQuery(id+"F0.wireOp",EDGE,"E5.MirrorCS");var subQ2=sQuery(id+"F0.wireOp",EDGE,"E1");Q16=makeQuery(id+"F18.opFillet","BLEND_EDGE",EDGE,{"blendedFrom":[makeQuery(id+"F1.opExtrude","CAP_EDGE",EDGE,{"disambiguationData":[OSD([subQ2,subQ1])],"isStart":true}),makeQuery(id+"F5.boolean.opBoolean","COPY",FACE,{"disambiguationData":[TD([makeQuery(id+"F1.opExtrude","SWEPT_FACE",FACE,{"disambiguationData":[OSD([subQ2,subQ1])]})])],"derivedFrom":makeQuery(id+"F5.opExtrude","SWEPT_FACE",FACE,{"disambiguationData":[OSD([sQuery(id+"F4.wireOp",EDGE,"E14")])]})})],"blendedInto":[makeQuery(id+"F5.boolean.opBoolean","COPY",FACE,{"disambiguationData":[TD([makeQuery(id+"F1.opExtrude","SWEPT_FACE",FACE,{"disambiguationData":[OSD([subQ2,subQ1])]})])],"derivedFrom":makeQuery(id+"F5.opExtrude","SWEPT_FACE",FACE,{"disambiguationData":[OSD([sQuery(id+"F4.wireOp",EDGE,"E14")])]})})]});}
            var Q17;
            {var subQ1=sQuery(id+"F0.wireOp",EDGE,"E1");var subQ2=sQuery(id+"F0.wireOp",EDGE,"E3");Q17=makeQuery(id+"F18.opFillet","BLEND_EDGE",EDGE,{"blendedFrom":[makeQuery(id+"F1.opExtrude","SWEPT_EDGE",EDGE,{"disambiguationData":[OSD([subQ1,subQ2])]}),makeQuery(id+"F5.boolean.opBoolean","COPY",FACE,{"disambiguationData":[TD([makeQuery(id+"F1.opExtrude","SWEPT_FACE",FACE,{"disambiguationData":[OSD([subQ1,sQuery(id+"F0.wireOp",EDGE,"E5.MirrorCS")])]})])],"derivedFrom":makeQuery(id+"F5.opExtrude","SWEPT_FACE",FACE,{"disambiguationData":[OSD([sQuery(id+"F4.wireOp",EDGE,"E14")])]})})],"blendedInto":[makeQuery(id+"F5.boolean.opBoolean","COPY",FACE,{"disambiguationData":[TD([makeQuery(id+"F1.opExtrude","SWEPT_FACE",FACE,{"disambiguationData":[OSD([subQ1,sQuery(id+"F0.wireOp",EDGE,"E5.MirrorCS")])]})])],"derivedFrom":makeQuery(id+"F5.opExtrude","SWEPT_FACE",FACE,{"disambiguationData":[OSD([sQuery(id+"F4.wireOp",EDGE,"E14")])]})})]});}
            var Q18;
            {var subQ1=sQuery(id+"F0.wireOp",EDGE,"E5.MirrorCS");var subQ2=sQuery(id+"F0.wireOp",EDGE,"E1");Q18=makeQuery(id+"F18.opFillet","BLEND_EDGE",EDGE,{"blendedFrom":[makeQuery(id+"F1.opExtrude","CAP_EDGE",EDGE,{"disambiguationData":[OSD([subQ2,subQ1])],"isStart":false}),makeQuery(id+"F5.boolean.opBoolean","COPY",FACE,{"disambiguationData":[TD([makeQuery(id+"F1.opExtrude","SWEPT_FACE",FACE,{"disambiguationData":[OSD([subQ2,subQ1])]})])],"derivedFrom":makeQuery(id+"F5.opExtrude","SWEPT_FACE",FACE,{"disambiguationData":[OSD([sQuery(id+"F4.wireOp",EDGE,"E14")])]})})],"blendedInto":[makeQuery(id+"F5.boolean.opBoolean","COPY",FACE,{"disambiguationData":[TD([makeQuery(id+"F1.opExtrude","SWEPT_FACE",FACE,{"disambiguationData":[OSD([subQ2,subQ1])]})])],"derivedFrom":makeQuery(id+"F5.opExtrude","SWEPT_FACE",FACE,{"disambiguationData":[OSD([sQuery(id+"F4.wireOp",EDGE,"E14")])]})})]});}
            var Q19;
            {var subQ1=sQuery(id+"F0.wireOp",EDGE,"E5.MirrorCS");var subQ3=sQuery(id+"F0.wireOp",EDGE,"E4.MirrorCS");Q19=makeQuery(id+"F18.opFillet","BLEND_EDGE",EDGE,{"blendedFrom":[makeQuery(id+"F1.opExtrude","SWEPT_EDGE",EDGE,{"disambiguationData":[OSD([subQ3,subQ1])]}),makeQuery(id+"F5.boolean.opBoolean","COPY",FACE,{"disambiguationData":[TD([makeQuery(id+"F1.opExtrude","SWEPT_FACE",FACE,{"disambiguationData":[OSD([sQuery(id+"F0.wireOp",EDGE,"E1"),subQ1])]})])],"derivedFrom":makeQuery(id+"F5.opExtrude","SWEPT_FACE",FACE,{"disambiguationData":[OSD([sQuery(id+"F4.wireOp",EDGE,"E14")])]})})],"blendedInto":[makeQuery(id+"F5.boolean.opBoolean","COPY",FACE,{"disambiguationData":[TD([makeQuery(id+"F1.opExtrude","SWEPT_FACE",FACE,{"disambiguationData":[OSD([sQuery(id+"F0.wireOp",EDGE,"E1"),subQ1])]})])],"derivedFrom":makeQuery(id+"F5.opExtrude","SWEPT_FACE",FACE,{"disambiguationData":[OSD([sQuery(id+"F4.wireOp",EDGE,"E14")])]})})]});}
            var Q20;
            {var subQ0=sQuery(id+"F0.wireOp",EDGE,"E0");var subQ1=makeQuery(id+"F1.opExtrude","SWEPT_FACE",FACE,{"disambiguationData":[OSD([subQ0])]});var subQ2=sQuery(id+"F0.wireOp",EDGE,"E3");Q20=makeQuery(id+"F18.opFillet","BLEND_EDGE",EDGE,{"blendedFrom":[makeQuery(id+"F1.opExtrude","CAP_EDGE",EDGE,{"disambiguationData":[OSD([subQ2])],"isStart":true}),makeQuery(id+"F3.boolean.opBoolean","SPLIT",FACE,{"disambiguationData":[TD([makeQuery(id+"F1.opExtrude","CAP_FACE",FACE,{"disambiguationData":[OSD([subQ0,sQuery(id+"F0.wireOp",EDGE,"E1"),sQuery(id+"F0.wireOp",EDGE,"E2.MirrorCS"),subQ2,sQuery(id+"F0.wireOp",EDGE,"E4.MirrorCS"),sQuery(id+"F0.wireOp",EDGE,"E5.MirrorCS"),sQuery(id+"F0.wireOp",EDGE,"E6.MirrorCS")])],"isStart":true})])],"derivedFrom":subQ1})],"blendedInto":[makeQuery(id+"F3.boolean.opBoolean","SPLIT",FACE,{"disambiguationData":[TD([makeQuery(id+"F1.opExtrude","CAP_FACE",FACE,{"disambiguationData":[OSD([subQ0,sQuery(id+"F0.wireOp",EDGE,"E1"),sQuery(id+"F0.wireOp",EDGE,"E2.MirrorCS"),subQ2,sQuery(id+"F0.wireOp",EDGE,"E4.MirrorCS"),sQuery(id+"F0.wireOp",EDGE,"E5.MirrorCS"),sQuery(id+"F0.wireOp",EDGE,"E6.MirrorCS")])],"isStart":true})])],"derivedFrom":subQ1})]});}
            var Q21;
            {var subQ0=sQuery(id+"F0.wireOp",EDGE,"E0");var subQ1=makeQuery(id+"F1.opExtrude","SWEPT_FACE",FACE,{"disambiguationData":[OSD([subQ0])]});var subQ2=sQuery(id+"F0.wireOp",EDGE,"E5.MirrorCS");var subQ3=sQuery(id+"F0.wireOp",EDGE,"E1");Q21=makeQuery(id+"F18.opFillet","BLEND_EDGE",EDGE,{"blendedFrom":[makeQuery(id+"F1.opExtrude","CAP_EDGE",EDGE,{"disambiguationData":[OSD([subQ3,subQ2])],"isStart":true}),makeQuery(id+"F3.boolean.opBoolean","SPLIT",FACE,{"disambiguationData":[TD([makeQuery(id+"F1.opExtrude","CAP_FACE",FACE,{"disambiguationData":[OSD([subQ0,subQ3,sQuery(id+"F0.wireOp",EDGE,"E2.MirrorCS"),sQuery(id+"F0.wireOp",EDGE,"E3"),sQuery(id+"F0.wireOp",EDGE,"E4.MirrorCS"),subQ2,sQuery(id+"F0.wireOp",EDGE,"E6.MirrorCS")])],"isStart":true})])],"derivedFrom":subQ1})],"blendedInto":[makeQuery(id+"F3.boolean.opBoolean","SPLIT",FACE,{"disambiguationData":[TD([makeQuery(id+"F1.opExtrude","CAP_FACE",FACE,{"disambiguationData":[OSD([subQ0,subQ3,sQuery(id+"F0.wireOp",EDGE,"E2.MirrorCS"),sQuery(id+"F0.wireOp",EDGE,"E3"),sQuery(id+"F0.wireOp",EDGE,"E4.MirrorCS"),subQ2,sQuery(id+"F0.wireOp",EDGE,"E6.MirrorCS")])],"isStart":true})])],"derivedFrom":subQ1})]});}
            var Q22;
            {var subQ0=sQuery(id+"F0.wireOp",EDGE,"E0");var subQ1=makeQuery(id+"F1.opExtrude","SWEPT_FACE",FACE,{"disambiguationData":[OSD([subQ0])]});var subQ2=sQuery(id+"F0.wireOp",EDGE,"E4.MirrorCS");Q22=makeQuery(id+"F18.opFillet","BLEND_EDGE",EDGE,{"blendedFrom":[makeQuery(id+"F1.opExtrude","CAP_EDGE",EDGE,{"disambiguationData":[OSD([subQ2])],"isStart":true}),makeQuery(id+"F3.boolean.opBoolean","SPLIT",FACE,{"disambiguationData":[TD([makeQuery(id+"F1.opExtrude","CAP_FACE",FACE,{"disambiguationData":[OSD([subQ0,sQuery(id+"F0.wireOp",EDGE,"E1"),sQuery(id+"F0.wireOp",EDGE,"E2.MirrorCS"),sQuery(id+"F0.wireOp",EDGE,"E3"),subQ2,sQuery(id+"F0.wireOp",EDGE,"E5.MirrorCS"),sQuery(id+"F0.wireOp",EDGE,"E6.MirrorCS")])],"isStart":true})])],"derivedFrom":subQ1})],"blendedInto":[makeQuery(id+"F3.boolean.opBoolean","SPLIT",FACE,{"disambiguationData":[TD([makeQuery(id+"F1.opExtrude","CAP_FACE",FACE,{"disambiguationData":[OSD([subQ0,sQuery(id+"F0.wireOp",EDGE,"E1"),sQuery(id+"F0.wireOp",EDGE,"E2.MirrorCS"),sQuery(id+"F0.wireOp",EDGE,"E3"),subQ2,sQuery(id+"F0.wireOp",EDGE,"E5.MirrorCS"),sQuery(id+"F0.wireOp",EDGE,"E6.MirrorCS")])],"isStart":true})])],"derivedFrom":subQ1})]});}
            var Q23;
            {var subQ0=sQuery(id+"F0.wireOp",EDGE,"E0");var subQ1=makeQuery(id+"F1.opExtrude","SWEPT_FACE",FACE,{"disambiguationData":[OSD([subQ0])]});var subQ2=sQuery(id+"F0.wireOp",EDGE,"E6.MirrorCS");var subQ3=sQuery(id+"F0.wireOp",EDGE,"E2.MirrorCS");Q23=makeQuery(id+"F18.opFillet","BLEND_EDGE",EDGE,{"blendedFrom":[makeQuery(id+"F1.opExtrude","CAP_EDGE",EDGE,{"disambiguationData":[OSD([subQ3,subQ2])],"isStart":true}),makeQuery(id+"F3.boolean.opBoolean","SPLIT",FACE,{"disambiguationData":[TD([makeQuery(id+"F1.opExtrude","CAP_FACE",FACE,{"disambiguationData":[OSD([subQ0,sQuery(id+"F0.wireOp",EDGE,"E1"),subQ3,sQuery(id+"F0.wireOp",EDGE,"E3"),sQuery(id+"F0.wireOp",EDGE,"E4.MirrorCS"),sQuery(id+"F0.wireOp",EDGE,"E5.MirrorCS"),subQ2])],"isStart":true})])],"derivedFrom":subQ1})],"blendedInto":[makeQuery(id+"F3.boolean.opBoolean","SPLIT",FACE,{"disambiguationData":[TD([makeQuery(id+"F1.opExtrude","CAP_FACE",FACE,{"disambiguationData":[OSD([subQ0,sQuery(id+"F0.wireOp",EDGE,"E1"),subQ3,sQuery(id+"F0.wireOp",EDGE,"E3"),sQuery(id+"F0.wireOp",EDGE,"E4.MirrorCS"),sQuery(id+"F0.wireOp",EDGE,"E5.MirrorCS"),subQ2])],"isStart":true})])],"derivedFrom":subQ1})]});}
            fillet(context, id + "F19", {"entities" : qUnion([Q0, Q1, Q2, Q3, Q4, Q5, Q6, Q7, Q8, Q9, Q10, Q11, Q12, Q13, Q14, Q15, Q16, Q17, Q18, Q19, Q20, Q21, Q22, Q23]), "radius" : 0.5 * mm, "tangentPropagation" : true, "allowEdgeOverflow" : false});
        }
        {
            var Q0;
            Q0=makeQuery(id+"F17.opExtrude","CAP_EDGE",EDGE,{"disambiguationData":[OSD([sQuery(id+"F16.wireOp",EDGE,"E30")])],"isStart":false});
            var Q1;
            Q1=makeQuery(id+"F13.opExtrude","CAP_EDGE",EDGE,{"disambiguationData":[OSD([sQuery(id+"F12.wireOp",EDGE,"E26")])],"isStart":false});
            var Q2;
            Q2=makeQuery(id+"F7.opExtrude","CAP_EDGE",EDGE,{"disambiguationData":[OSD([sQuery(id+"F6.wireOp",EDGE,"E20")])],"isStart":false});
            var Q3;
            Q3=makeQuery(id+"F15.opExtrude","CAP_EDGE",EDGE,{"disambiguationData":[OSD([sQuery(id+"F14.wireOp",EDGE,"E28")])],"isStart":false});
            var Q4;
            Q4=makeQuery(id+"F11.opExtrude","CAP_EDGE",EDGE,{"disambiguationData":[OSD([sQuery(id+"F10.wireOp",EDGE,"E24")])],"isStart":false});
            var Q5;
            Q5=makeQuery(id+"F9.opExtrude","CAP_EDGE",EDGE,{"disambiguationData":[OSD([sQuery(id+"F8.wireOp",EDGE,"E22")])],"isStart":false});
            fillet(context, id + "F20", {"entities" : qUnion([Q0, Q1, Q2, Q3, Q4, Q5]), "radius" : 0.5 * mm, "tangentPropagation" : true, "allowEdgeOverflow" : false});
        }
    });
